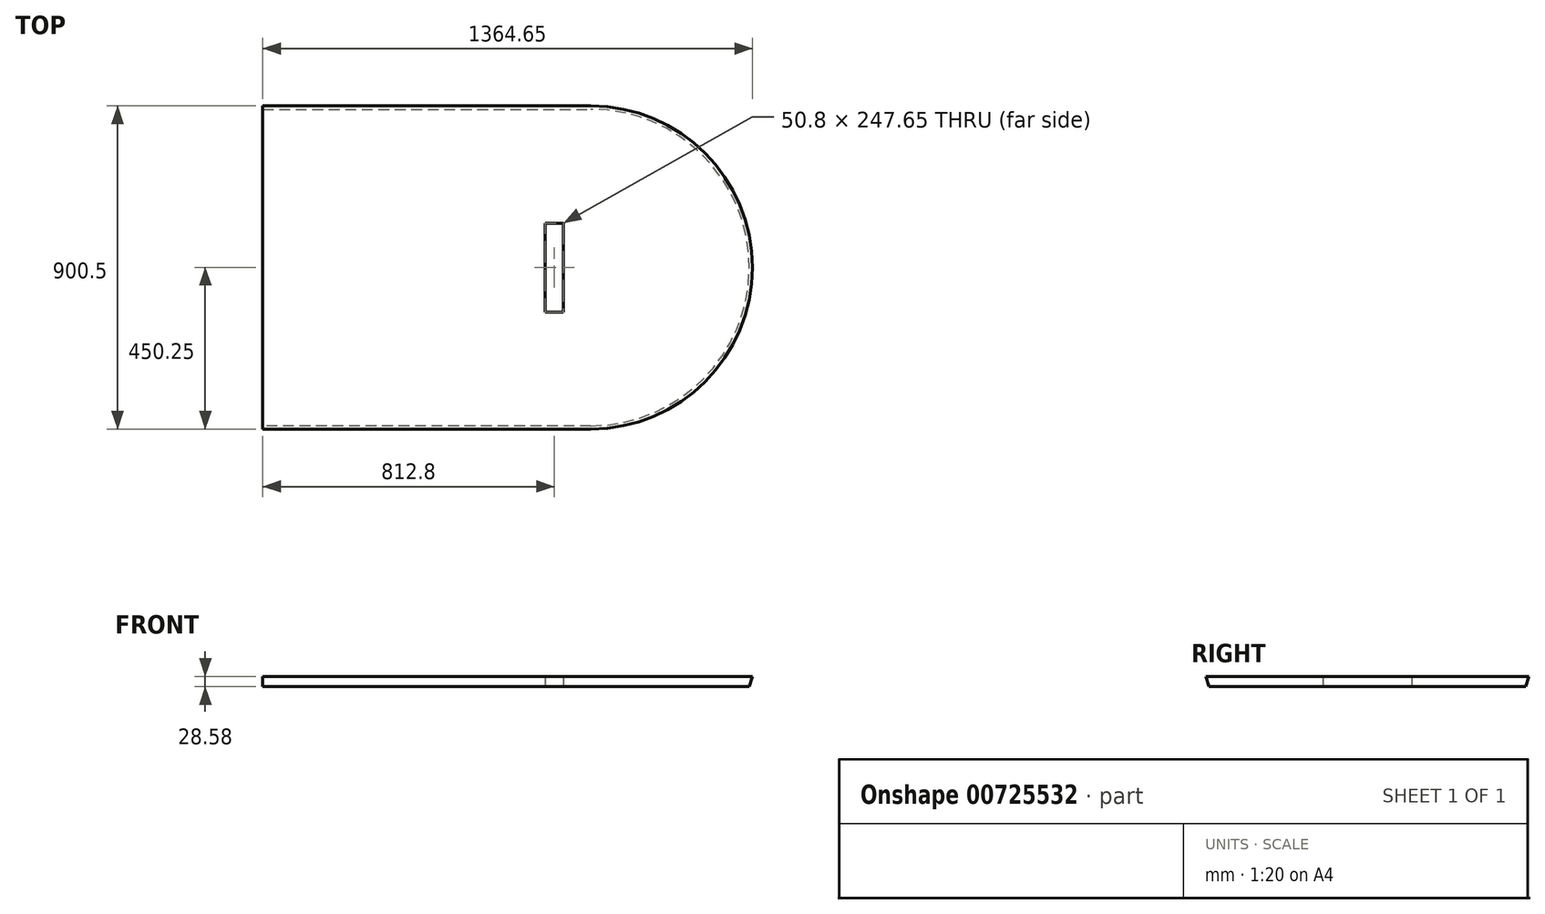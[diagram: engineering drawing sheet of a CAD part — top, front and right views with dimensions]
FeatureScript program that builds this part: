
annotation { "Feature Type Name" : "Feature", "Feature Type Description" : "" }
export const myFeature = defineFeature(function(context is Context, id is Id, definition is map)
    precondition{}
    {
        {
            var Q0;
            Q0=qCreatedBy(makeId("Top.planeOp"),FACE);
            var sketch = newSketch(context, id + "F0", { "sketchPlane" : qUnion([Q0])});
            skLineSegment(sketch, "E0.bottom", {"start": v(-685.8, 457.2) * mm, "end": v(685.8, 457.2) * mm});
            skLineSegment(sketch, "E0.top", {"start": v(-685.8, -457.2) * mm, "end": v(685.8, -457.2) * mm});
            skLineSegment(sketch, "E0.left", {"start": v(-685.8, 457.2) * mm, "end": v(-685.8, -457.2) * mm});
            skLineSegment(sketch, "E0.right", {"start": v(685.8, 457.2) * mm, "end": v(685.8, -457.2) * mm});
            skPoint(sketch, "E0.middle", {"position": v(0, 0) * mm});
            skLineSegment(sketch, "E1", {"start": v(685.8, 0) * mm, "end": v(228.6, 0) * mm});
            skArc(sketch, "E2", {"start": v(228.6, 457.2) * mm, "mid": v(685.8, 0) * mm, "end": v(228.6, -457.2) * mm});
            skLineSegment(sketch, "E3", {"start": v(228.6, 0) * mm, "end": v(127, 0) * mm});
            skLineSegment(sketch, "E4.bottom", {"start": v(152.4, 123.83) * mm, "end": v(101.6, 123.83) * mm});
            skLineSegment(sketch, "E4.top", {"start": v(152.4, -123.82) * mm, "end": v(101.6, -123.82) * mm});
            skLineSegment(sketch, "E4.left", {"start": v(152.4, 123.83) * mm, "end": v(152.4, -123.82) * mm});
            skLineSegment(sketch, "E4.right", {"start": v(101.6, 123.83) * mm, "end": v(101.6, -123.82) * mm});
            skPoint(sketch, "E4.middle", {"position": v(127, 0) * mm});
            skSolve(sketch);
        }
        {
            var Q0;
            {var subQ0=sQuery(id+"F0.wireOp",EDGE,"E0.left");Q0=makeQuery(id+"F0.imprint","IMPRINT",FACE,{"disambiguationData":[TD([[makeQuery(id+"F0.imprint","IMPRINT",EDGE,{"derivedFrom":subQ0}),1.0]])]});}
            extrude(context, id + "F1", {"entities" : qUnion([Q0]), "depth" : 28.57 * mm, "offsetDistance" : 25.4 * mm});
        }
        {
            var Q0;
            Q0=makeQuery(id+"F1.opExtrude","CAP_EDGE",EDGE,{"disambiguationData":[OSD([sQuery(id+"F0.wireOp",EDGE,"E0.bottom")])],"isStart":true});
            var Q1;
            Q1=makeQuery(id+"F1.opExtrude","CAP_EDGE",EDGE,{"disambiguationData":[OSD([sQuery(id+"F0.wireOp",EDGE,"E2")])],"isStart":true});
            var Q2;
            Q2=makeQuery(id+"F1.opExtrude","CAP_EDGE",EDGE,{"disambiguationData":[OSD([sQuery(id+"F0.wireOp",EDGE,"E0.top")])],"isStart":true});
            chamfer(context, id + "F2", {"entities" : qUnion([Q0, Q1, Q2]), "chamferType" : ChamferType.TWO_OFFSETS, "width1" : 50.8 * mm, "oppositeDirection" : false, "width2" : 15.88 * mm, "tangentPropagation" : true});
        }
    });
